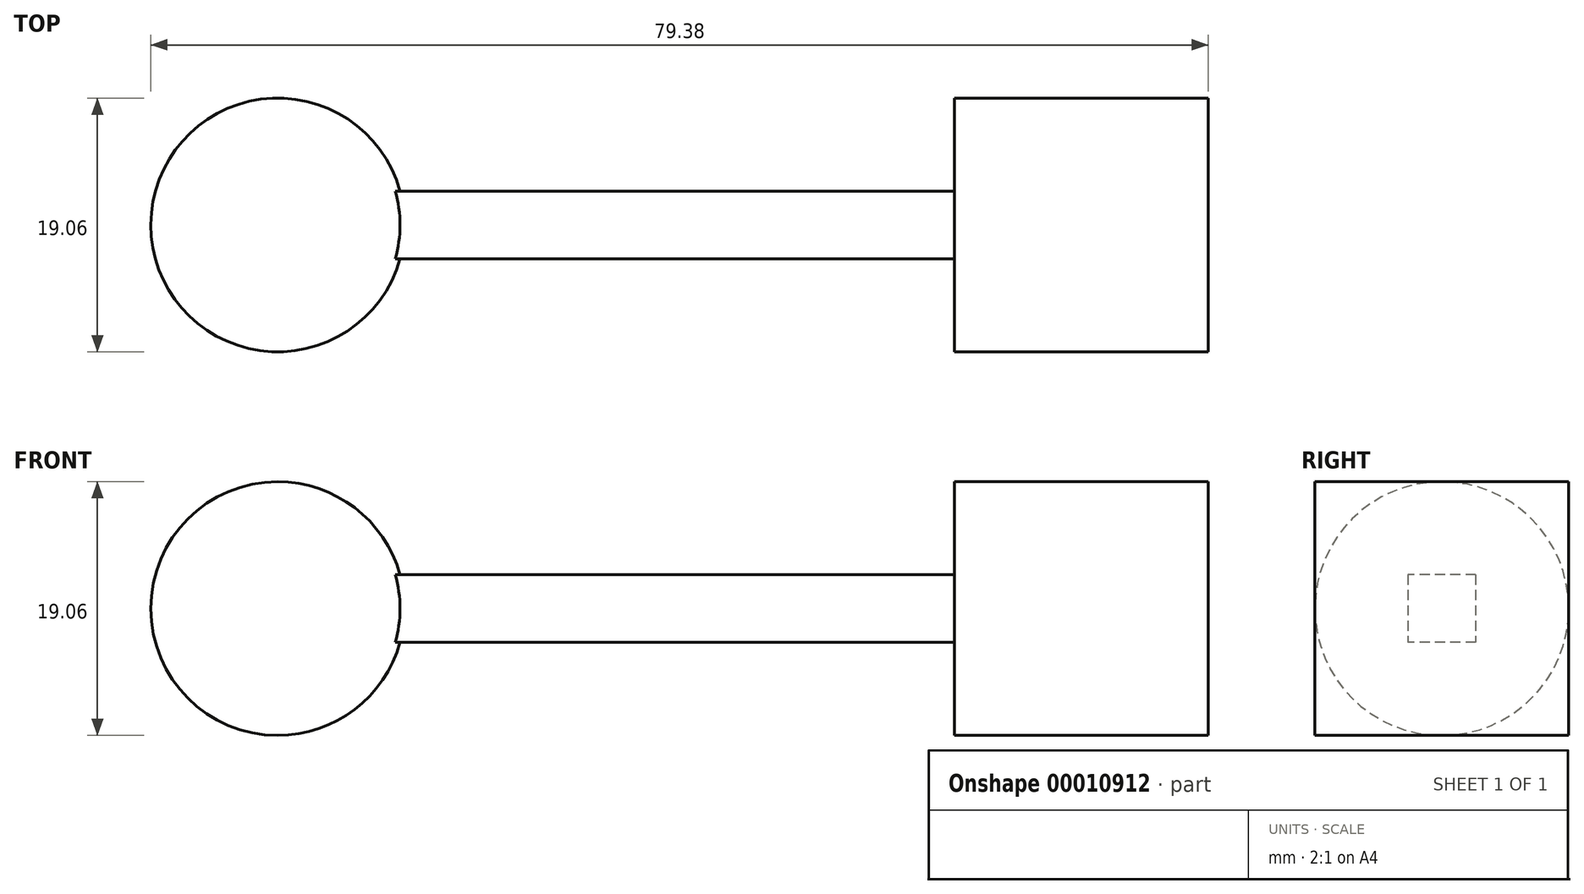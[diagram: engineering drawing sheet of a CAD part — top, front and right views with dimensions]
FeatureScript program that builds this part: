
annotation { "Feature Type Name" : "Feature", "Feature Type Description" : "" }
export const myFeature = defineFeature(function(context is Context, id is Id, definition is map)
    precondition{}
    {
        {
            var Q0;
            Q0=qCreatedBy(makeId("Front.planeOp"),FACE);
            var sketch = newSketch(context, id + "F0", { "sketchPlane" : qUnion([Q0])});
            skCircle(sketch, "E0", {"center": v(0, 0) * mm, "radius": 9.53 * mm});
            skLineSegment(sketch, "E1", {"start": v(0, 9.53) * mm, "end": v(0, -9.53) * mm});
            skSolve(sketch);
        }
        {
            var Q0;
            {var subQ0=sQuery(id+"F0.wireOp",EDGE,"E1");Q0=makeQuery(id+"F0.imprint","IMPRINT",FACE,{"disambiguationData":[TD([[makeQuery(id+"F0.imprint","IMPRINT",EDGE,{"derivedFrom":subQ0}),1.0]])]});}
            var Q1;
            Q1=sQuery(id+"F0.wireOp",EDGE,"E1");
            revolve(context, id + "F1", {"entities" : qUnion([Q0]), "axis" : qUnion([Q1]), "revolveType" : RevolveType.FULL});
        }
        {
            var Q0;
            Q0=qCreatedBy(makeId("Right.planeOp"),FACE);
            var sketch = newSketch(context, id + "F2", { "sketchPlane" : qUnion([Q0])});
            skLineSegment(sketch, "E2.bottom", {"start": v(2.54, 2.54) * mm, "end": v(-2.54, 2.54) * mm});
            skLineSegment(sketch, "E2.top", {"start": v(2.54, -2.54) * mm, "end": v(-2.54, -2.54) * mm});
            skLineSegment(sketch, "E2.left", {"start": v(2.54, 2.54) * mm, "end": v(2.54, -2.54) * mm});
            skLineSegment(sketch, "E2.right", {"start": v(-2.54, 2.54) * mm, "end": v(-2.54, -2.54) * mm});
            skPoint(sketch, "E3", {"position": v(0, 2.54) * mm});
            skPoint(sketch, "E4", {"position": v(2.54, 0) * mm});
            skPoint(sketch, "E5", {"position": v(0, 0) * mm});
            skSolve(sketch);
        }
        {
            var Q0;
            Q0 = qSketchRegion(id + "F2", true);
            extrude(context, id + "F3", {"entities" : qUnion([Q0]), "operationType" : NewBodyOperationType.ADD, "depth" : 50.8 * mm});
        }
        {
            var Q0;
            Q0=makeQuery(id+"F3.opExtrude","CAP_FACE",FACE,{"disambiguationData":[OSD([sQuery(id+"F2.wireOp",EDGE,"E2.bottom"),sQuery(id+"F2.wireOp",EDGE,"E2.top"),sQuery(id+"F2.wireOp",EDGE,"E2.left"),sQuery(id+"F2.wireOp",EDGE,"E2.right")])],"isStart":false});
            var sketch = newSketch(context, id + "F4", { "sketchPlane" : qUnion([Q0])});
            skLineSegment(sketch, "E6.bottom", {"start": v(-9.53, 9.53) * mm, "end": v(9.52, 9.53) * mm});
            skLineSegment(sketch, "E6.top", {"start": v(-9.52, -9.53) * mm, "end": v(9.53, -9.53) * mm});
            skLineSegment(sketch, "E6.left", {"start": v(-9.52, 9.52) * mm, "end": v(-9.52, -9.53) * mm});
            skLineSegment(sketch, "E6.right", {"start": v(9.52, 9.52) * mm, "end": v(9.52, -9.52) * mm});
            skPoint(sketch, "E7", {"position": v(0, 9.53) * mm});
            skPoint(sketch, "E8", {"position": v(-9.52, 0) * mm});
            skPoint(sketch, "E9", {"position": v(0, 0) * mm});
            skSolve(sketch);
        }
        {
            var Q0;
            Q0 = qSketchRegion(id + "F4", true);
            extrude(context, id + "F5", {"entities" : qUnion([Q0]), "operationType" : NewBodyOperationType.ADD, "depth" : 19.05 * mm});
        }
    });
